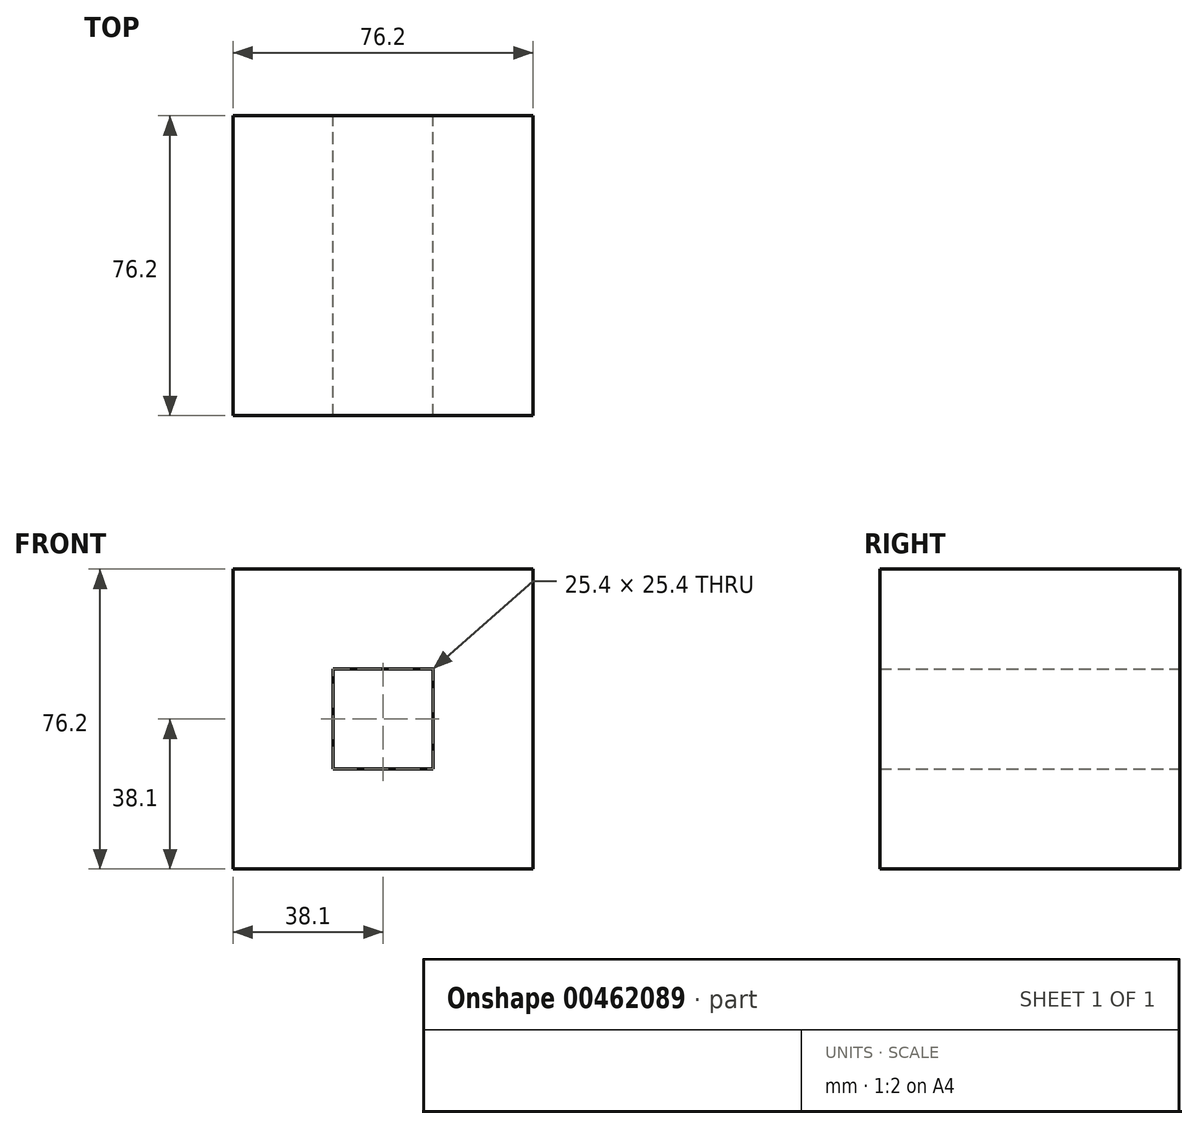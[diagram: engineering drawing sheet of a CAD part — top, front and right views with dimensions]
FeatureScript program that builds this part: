
annotation { "Feature Type Name" : "Feature", "Feature Type Description" : "" }
export const myFeature = defineFeature(function(context is Context, id is Id, definition is map)
    precondition{}
    {
        {
            var Q0;
            Q0=qCreatedBy(makeId("Front.planeOp"),FACE);
            var sketch = newSketch(context, id + "F0", { "sketchPlane" : qUnion([Q0])});
            skLineSegment(sketch, "E0.bottom", {"start": v(38.1, 38.1) * mm, "end": v(-38.1, 38.1) * mm});
            skLineSegment(sketch, "E0.top", {"start": v(38.1, -38.1) * mm, "end": v(-38.1, -38.1) * mm});
            skLineSegment(sketch, "E0.left", {"start": v(38.1, 38.1) * mm, "end": v(38.1, -38.1) * mm});
            skLineSegment(sketch, "E0.right", {"start": v(-38.1, 38.1) * mm, "end": v(-38.1, -38.1) * mm});
            skPoint(sketch, "E0.middle", {"position": v(0, 0) * mm});
            skLineSegment(sketch, "E1.bottom", {"start": v(12.7, 12.7) * mm, "end": v(-12.7, 12.7) * mm});
            skLineSegment(sketch, "E1.top", {"start": v(12.7, -12.7) * mm, "end": v(-12.7, -12.7) * mm});
            skLineSegment(sketch, "E1.left", {"start": v(12.7, 12.7) * mm, "end": v(12.7, -12.7) * mm});
            skLineSegment(sketch, "E1.right", {"start": v(-12.7, 12.7) * mm, "end": v(-12.7, -12.7) * mm});
            skSolve(sketch);
        }
        {
            var Q0;
            Q0 = qSketchRegion(id + "F0", true);
            extrude(context, id + "F1", {"entities" : qUnion([Q0]), "depth" : 76.2 * mm});
        }
    });
